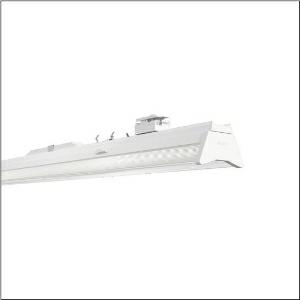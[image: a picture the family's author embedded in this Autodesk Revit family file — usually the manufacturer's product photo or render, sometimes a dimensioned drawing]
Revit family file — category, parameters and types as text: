
# Revit family: licross_r__11_performance_tw_51td16tnt85x_7c56
name_source: partatom
category: Lighting Fixtures
units: mm (PartAtom-declared; Revit-internal decimal feet)

## family parameters
Cut with Voids When Loaded = No
Host = Face
Light Source = No
Part Type = Normal
Room Calculation Point = No
Round Connector Dimension = Use Diameter
Shared = No

## types (1)
- --- (1 x LED 2700 K ... 6500 K, 8930 lm, 56 W, 2700K)
    Apparent Load = 56 VA
    CIE Flux Codes = 63 87 95 78 100
    Color Rendering = 80
    Color Temperature = 2700K
    Default Elevation = 1800 mm
    Description = Licross® 11 Performance TW, luminaire insert, of sheet steel, galvanised, coil coated, white, length: 1.500mm, width: 120mm, height: 123mm, LED rated luminous flux: 8.930lm, light colour: 8tw, control gear: DALI DT8, with plug, 5-pole, with phase selection, mains connection: 220..240V, AC, 50/60Hz, rated input power: 56W, halogen-free wiring, primary light control with lens, of plastic, primary optical cover: cover, of PMMA, light emission: direct/indirect distribution, primary light characteristic: symmetric, protection rating (complete): IP54, insulation class (complete): insulation class I (protective earthing), certification: CE, ENEC, VDE, UKCA, protection symbol: D if used in an environment with non-conductive dust loads with corresponding accessories, impact resistance: IK06, permissible ambient temperature for indoor applications: -25..+35°C, corresponds to IFS (International Featured Standards) requirements for safety and quality in the food industry, reducing of maximum allowable ambient temperature of 5°C with ceiling mounting, LABS conformity tested according to VDMA 24364:2018-05, packaging unit: 1 piece
    Height = 114 mm
    Lamp = 1 x LED 2700 K ... 6500 K
    Lamp Light Flux = 8930 lm
    Lamp Power = 56 W
    Lamp count = 1
    Length = 1500 mm
    Luminous efficacy = 159 lm/W
    Manufacturer = Siteco
    ModVariant = No
    Model = 51TD16TNT85X
    Mounting Place = Ceiling
    Mounting Type = Pendant
    Number of Poles = 1
    OnlyDefault = Yes
    Power Factor = 1
    Product Name = Licross® 11 Performance TW
    Product group = luminaire insert
    ProductGroupID = 902
    Protection Class = Protection class I
    Protection Degree = IP 54
    RLX_Detail_Level = 1
    RLX_Emergency_Light_Flux = 0 lm
    RLX_Emergency_Type = 0
    RLX_Emergency_Type_DB = No
    RlxData = <blob elided: 30333 chars, md5=f1a75ebd>
    Socket = socket
    Standby Power = 0 W
    System Light Flux = 8930 lm
    System Power = 56 W
    Type Comments = individual setting: CCT=2700K
    Type Image = l_1256138.jpg
    URL = http://relux.com
    VarID = @adj_049498
    Voltage = 0 V
    Weight = 0.00 kg
    Width = 120 mm

## geometry (parser evidence)
native form markers: Blend x4, Sweep x13
no freeform markers — native parametric forms only
